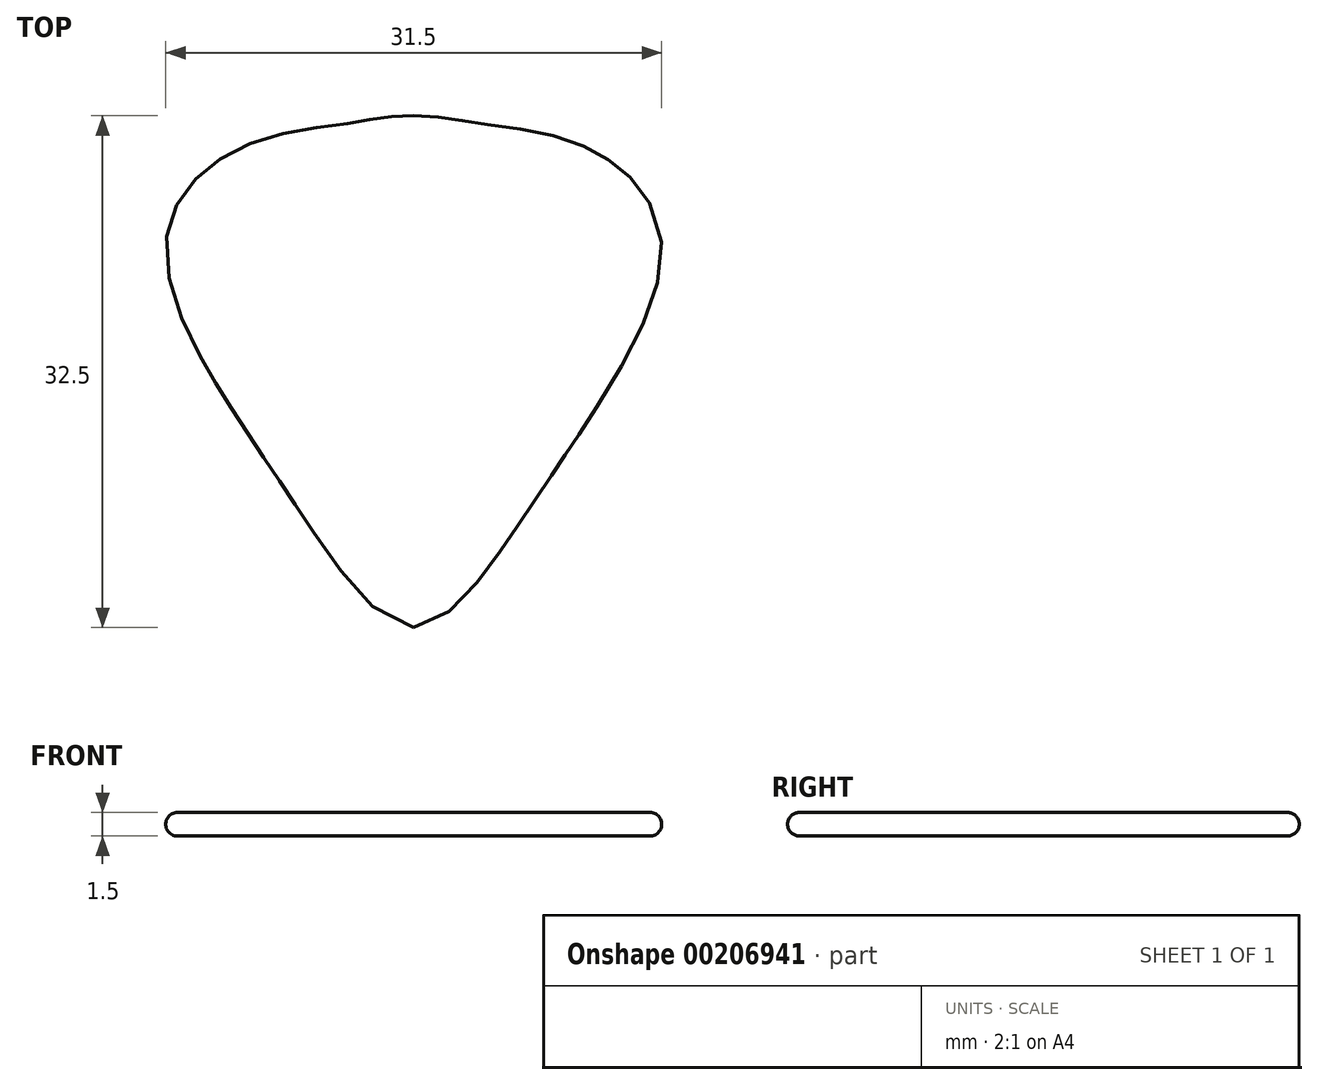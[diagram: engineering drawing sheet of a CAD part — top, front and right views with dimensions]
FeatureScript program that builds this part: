
annotation { "Feature Type Name" : "Feature", "Feature Type Description" : "" }
export const myFeature = defineFeature(function(context is Context, id is Id, definition is map)
    precondition{}
    {
        {
            var Q0;
            Q0=qCreatedBy(makeId("Top.planeOp"),FACE);
            var sketch = newSketch(context, id + "F0", { "sketchPlane" : qUnion([Q0])});
            skPoint(sketch, "E0.middle", {"position": v(0, 0) * mm});
            skLineSegment(sketch, "E1.bottom", {"start": v(15, -15.5) * mm, "end": v(-15, -15.5) * mm, "construction": true});
            skLineSegment(sketch, "E1.top", {"start": v(15, 15.5) * mm, "end": v(-15, 15.5) * mm, "construction": true});
            skLineSegment(sketch, "E1.left", {"start": v(15, -15.5) * mm, "end": v(15, 15.5) * mm, "construction": true});
            skLineSegment(sketch, "E1.right", {"start": v(-15, -15.5) * mm, "end": v(-15, 15.5) * mm, "construction": true});
            skFitSpline(sketch, "E2", {"points": [v(0, 15.5) * mm, v(-3.8, 15.07) * mm, v(-10.5, 13.63) * mm, v(-15, 7.94) * mm, v(-10.07, -3.27) * mm, v(-6.3, -8.92) * mm, v(0, -15.5) * mm], "startDerivative": vector(-46.78, 0) * mm, "endDerivative": vector(31.22, 0) * mm});
            skFitSpline(sketch, "E3.MirrorCS", {"points": [v(0, 15.5) * mm, v(3.8, 15.07) * mm, v(10.5, 13.63) * mm, v(15, 7.94) * mm, v(10.07, -3.27) * mm, v(6.3, -8.92) * mm, v(0, -15.5) * mm], "startDerivative": vector(46.78, 0) * mm, "endDerivative": vector(-31.22, 0) * mm});
            skSolve(sketch);
        }
        {
            var Q0;
            Q0=makeQuery(id+"F0.imprint","IMPRINT",FACE,{"disambiguationData":[TD([[makeQuery(id+"F0.imprint","IMPRINT",EDGE,{"derivedFrom":sQuery(id+"F0.wireOp",EDGE,"E2")}),1.0]])]});
            extrude(context, id + "F1", {"entities" : qUnion([Q0]), "depth" : 1.5 * mm});
        }
        {
            var Q0;
            Q0=qCreatedBy(makeId("Right.planeOp"),FACE);
            var sketch = newSketch(context, id + "F2", { "sketchPlane" : qUnion([Q0])});
            skArc(sketch, "E4", {"start": v(15.5, 0) * mm, "mid": v(16.25, 0.75) * mm, "end": v(15.5, 1.5) * mm});
            skLineSegment(sketch, "E5", {"start": v(15.5, 0) * mm, "end": v(15.5, 1.5) * mm, "construction": true});
            skLineSegment(sketch, "E6", {"start": v(15.5, 1.5) * mm, "end": v(15.5, 0) * mm});
            skSolve(sketch);
        }
        {
            var Q0;
            Q0=makeQuery(id+"F2.imprint","IMPRINT",FACE,{"disambiguationData":[TD([[makeQuery(id+"F2.imprint","IMPRINT",EDGE,{"derivedFrom":sQuery(id+"F2.wireOp",EDGE,"E4")}),1.0]])]});
            var Q1;
            Q1=makeQuery(id+"F1.opExtrude","CAP_EDGE",EDGE,{"disambiguationData":[OSD([sQuery(id+"F0.wireOp",EDGE,"E2")])],"isStart":false});
            var Q2;
            Q2=makeQuery(id+"F1.opExtrude","CAP_EDGE",EDGE,{"disambiguationData":[OSD([sQuery(id+"F0.wireOp",EDGE,"E3.MirrorCS")])],"isStart":false});
            sweep(context, id + "F3", {"operationType" : NewBodyOperationType.ADD, "profiles" : qUnion([Q0]), "path" : qUnion([Q1, Q2])});
        }
    });
